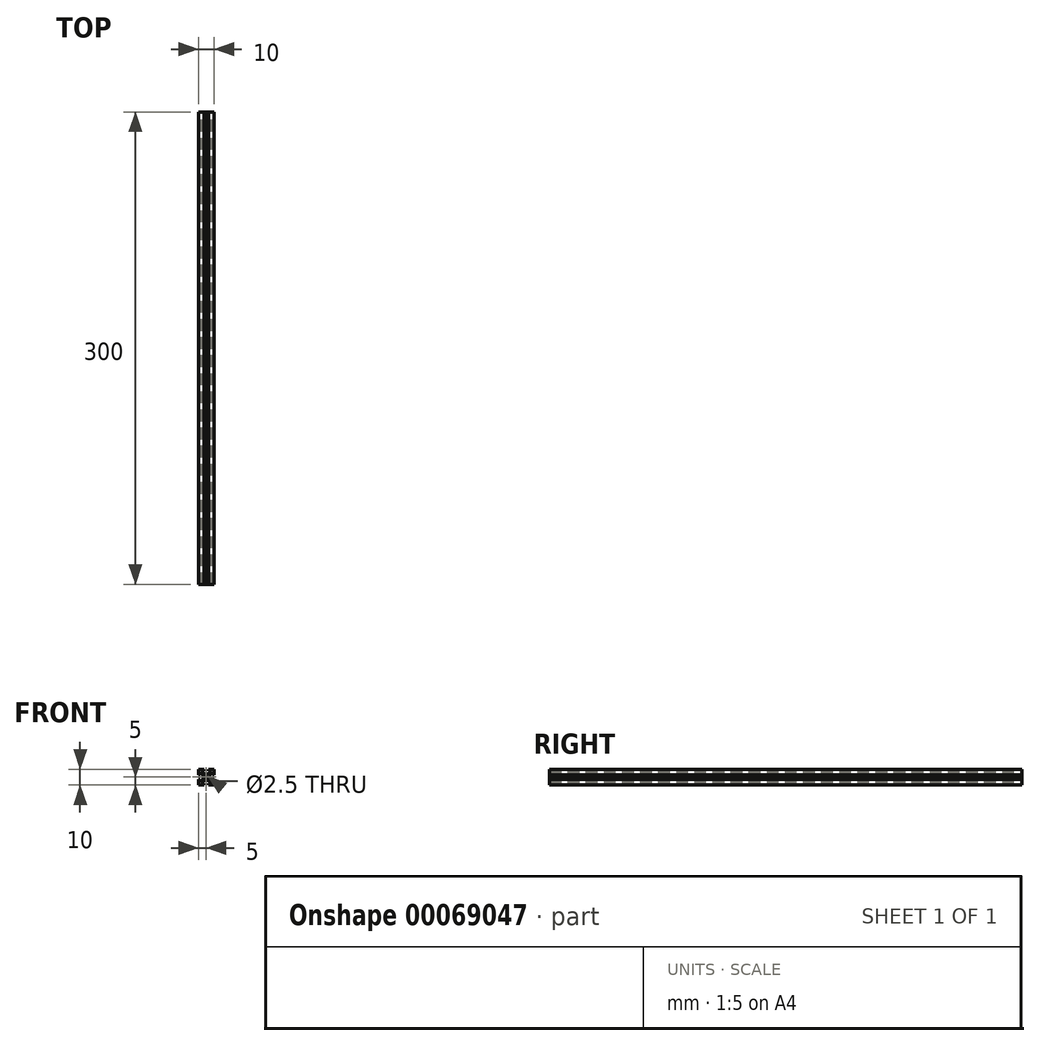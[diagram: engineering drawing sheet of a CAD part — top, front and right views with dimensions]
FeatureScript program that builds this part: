
annotation { "Feature Type Name" : "Feature", "Feature Type Description" : "" }
export const myFeature = defineFeature(function(context is Context, id is Id, definition is map)
    precondition{}
    {
        {
            var Q0;
            Q0=qCreatedBy(makeId("Front.planeOp"),FACE);
            var sketch = newSketch(context, id + "F0", { "sketchPlane" : qUnion([Q0])});
            skLineSegment(sketch, "E0", {"start": v(0, 0) * mm, "end": v(0, 3.5) * mm});
            skLineSegment(sketch, "E1", {"start": v(0, 3.5) * mm, "end": v(-1, 3.5) * mm});
            skLineSegment(sketch, "E2", {"start": v(-1, 3.5) * mm, "end": v(-1, 2) * mm});
            skLineSegment(sketch, "E3", {"start": v(-1, 2) * mm, "end": v(-3, 4) * mm});
            skLineSegment(sketch, "E4", {"start": v(-3, 4) * mm, "end": v(-3, 5) * mm});
            skLineSegment(sketch, "E5", {"start": v(-3, 5) * mm, "end": v(-5, 5) * mm, "construction": true});
            skLineSegment(sketch, "E6", {"start": v(-5, 5) * mm, "end": v(0, 0) * mm, "construction": true});
            skLineSegment(sketch, "E7.MirrorCS", {"start": v(-3.5, 0) * mm, "end": v(-3.5, 1) * mm});
            skLineSegment(sketch, "E8.MirrorCS", {"start": v(0, 0) * mm, "end": v(-3.5, 0) * mm});
            skLineSegment(sketch, "E9.MirrorCS", {"start": v(-3.5, 1) * mm, "end": v(-2, 1) * mm});
            skLineSegment(sketch, "E10.MirrorCS", {"start": v(-2, 1) * mm, "end": v(-4, 3) * mm});
            skLineSegment(sketch, "E11.MirrorCS", {"start": v(-4, 3) * mm, "end": v(-5, 3) * mm});
            skLineSegment(sketch, "E12.MirrorCS", {"start": v(-5, 3) * mm, "end": v(-5, 5) * mm, "construction": true});
            skLineSegment(sketch, "E13.1.0", {"start": v(-3, 6) * mm, "end": v(-3, 5) * mm});
            skLineSegment(sketch, "E13.1.1", {"start": v(-1, 8) * mm, "end": v(-3, 6) * mm});
            skLineSegment(sketch, "E13.1.2", {"start": v(-1, 6.5) * mm, "end": v(-1, 8) * mm});
            skLineSegment(sketch, "E13.1.3", {"start": v(0, 6.5) * mm, "end": v(-1, 6.5) * mm});
            skLineSegment(sketch, "E13.1.4", {"start": v(0, 10) * mm, "end": v(0, 6.5) * mm});
            skLineSegment(sketch, "E13.1.5", {"start": v(0, 10) * mm, "end": v(-3.5, 10) * mm});
            skLineSegment(sketch, "E13.1.6", {"start": v(-3.5, 10) * mm, "end": v(-3.5, 9) * mm});
            skLineSegment(sketch, "E13.1.7", {"start": v(-3.5, 9) * mm, "end": v(-2, 9) * mm});
            skLineSegment(sketch, "E13.1.8", {"start": v(-2, 9) * mm, "end": v(-4, 7) * mm});
            skLineSegment(sketch, "E13.1.9", {"start": v(-4, 7) * mm, "end": v(-5, 7) * mm});
            skLineSegment(sketch, "E13.2.0", {"start": v(-6, 7) * mm, "end": v(-5, 7) * mm});
            skLineSegment(sketch, "E13.2.1", {"start": v(-8, 9) * mm, "end": v(-6, 7) * mm});
            skLineSegment(sketch, "E13.2.2", {"start": v(-6.5, 9) * mm, "end": v(-8, 9) * mm});
            skLineSegment(sketch, "E13.2.3", {"start": v(-6.5, 10) * mm, "end": v(-6.5, 9) * mm});
            skLineSegment(sketch, "E13.2.4", {"start": v(-10, 10) * mm, "end": v(-6.5, 10) * mm});
            skLineSegment(sketch, "E13.2.5", {"start": v(-10, 10) * mm, "end": v(-10, 6.5) * mm});
            skLineSegment(sketch, "E13.2.6", {"start": v(-10, 6.5) * mm, "end": v(-9, 6.5) * mm});
            skLineSegment(sketch, "E13.2.7", {"start": v(-9, 6.5) * mm, "end": v(-9, 8) * mm});
            skLineSegment(sketch, "E13.2.8", {"start": v(-9, 8) * mm, "end": v(-7, 6) * mm});
            skLineSegment(sketch, "E13.2.9", {"start": v(-7, 6) * mm, "end": v(-7, 5) * mm});
            skLineSegment(sketch, "E13.3.0", {"start": v(-7, 4) * mm, "end": v(-7, 5) * mm});
            skLineSegment(sketch, "E13.3.1", {"start": v(-9, 2) * mm, "end": v(-7, 4) * mm});
            skLineSegment(sketch, "E13.3.2", {"start": v(-9, 3.5) * mm, "end": v(-9, 2) * mm});
            skLineSegment(sketch, "E13.3.3", {"start": v(-10, 3.5) * mm, "end": v(-9, 3.5) * mm});
            skLineSegment(sketch, "E13.3.4", {"start": v(-10, 0) * mm, "end": v(-10, 3.5) * mm});
            skLineSegment(sketch, "E13.3.5", {"start": v(-10, 0) * mm, "end": v(-6.5, 0) * mm});
            skLineSegment(sketch, "E13.3.6", {"start": v(-6.5, 0) * mm, "end": v(-6.5, 1) * mm});
            skLineSegment(sketch, "E13.3.7", {"start": v(-6.5, 1) * mm, "end": v(-8, 1) * mm});
            skLineSegment(sketch, "E13.3.8", {"start": v(-8, 1) * mm, "end": v(-6, 3) * mm});
            skLineSegment(sketch, "E13.3.9", {"start": v(-6, 3) * mm, "end": v(-5, 3) * mm});
            skPoint(sketch, "E13.center", {"position": v(-5, 5) * mm});
            skCircle(sketch, "E14", {"center": v(-5, 5) * mm, "radius": 1.25 * mm});
            skSolve(sketch);
        }
        {
            var Q0;
            Q0=makeQuery(id+"F0.imprint","IMPRINT",FACE,{"disambiguationData":[TD([[makeQuery(id+"F0.imprint","IMPRINT",EDGE,{"derivedFrom":sQuery(id+"F0.wireOp",EDGE,"E0")}),1.0]])]});
            extrude(context, id + "F1", {"entities" : qUnion([Q0]), "depth" : 300 * mm});
        }
    });
